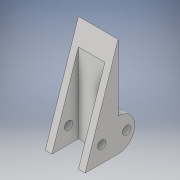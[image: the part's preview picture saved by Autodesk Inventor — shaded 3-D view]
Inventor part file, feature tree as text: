
AUTODESK INVENTOR PART (.ipt)
format: ipt  version: 2019 (Build 230136000, 136)  size: 156,160 bytes
history: native  units: in
note: dims shown in document units (in); Inventor stores cm internally (conversion verified against a paired STEP export)
features: extrude x7, sketch x7
ambient origin geometry x8: Origin, YZ Plane, XZ Plane, XY Plane, X Axis, Y Axis, Z Axis, Center Point
bodies: Body1 (feature_tree)
feature tree (14):
  extrude  "Extrusion2"  Depth=1.5in
  extrude  "Extrusion6"  Depth=0.1in
  extrude  "Extrusion7"  Depth=0.1in
  extrude  "Extrusion8"  Depth=0.4in TaperAngle=0.0deg
  extrude  "Extrusion9"  Depth=0.25in
  extrude  "Extrusion10"  Depth=0.125in
  extrude  "Extrusion11"  Depth=0.25in
  sketch  "Sketch1"  dims[d4=0.6in d5=1.5in]
  sketch  "Sketch8"  dims[d6=0.5in d7=0.0in d22=0.1in]
  sketch  "Sketch9"  dims[d23=0.1in d24=0.1in]
  sketch  "Sketch10"  dims[d25=0.4in d26=0.0in d27=2.0in d28=0.0in]
  sketch  "Sketch11"  dims[d29=0.1in d30=0.0in d31=0.25in]
  sketch  "Sketch12"  dims[d33=0.125in d34=0.0in d35=0.125in]
  sketch  "Sketch13"  dims[d36=0.125in d37=0.0in d38=0.25in d39=0.125in d40=2.0in d41=0.0in]
